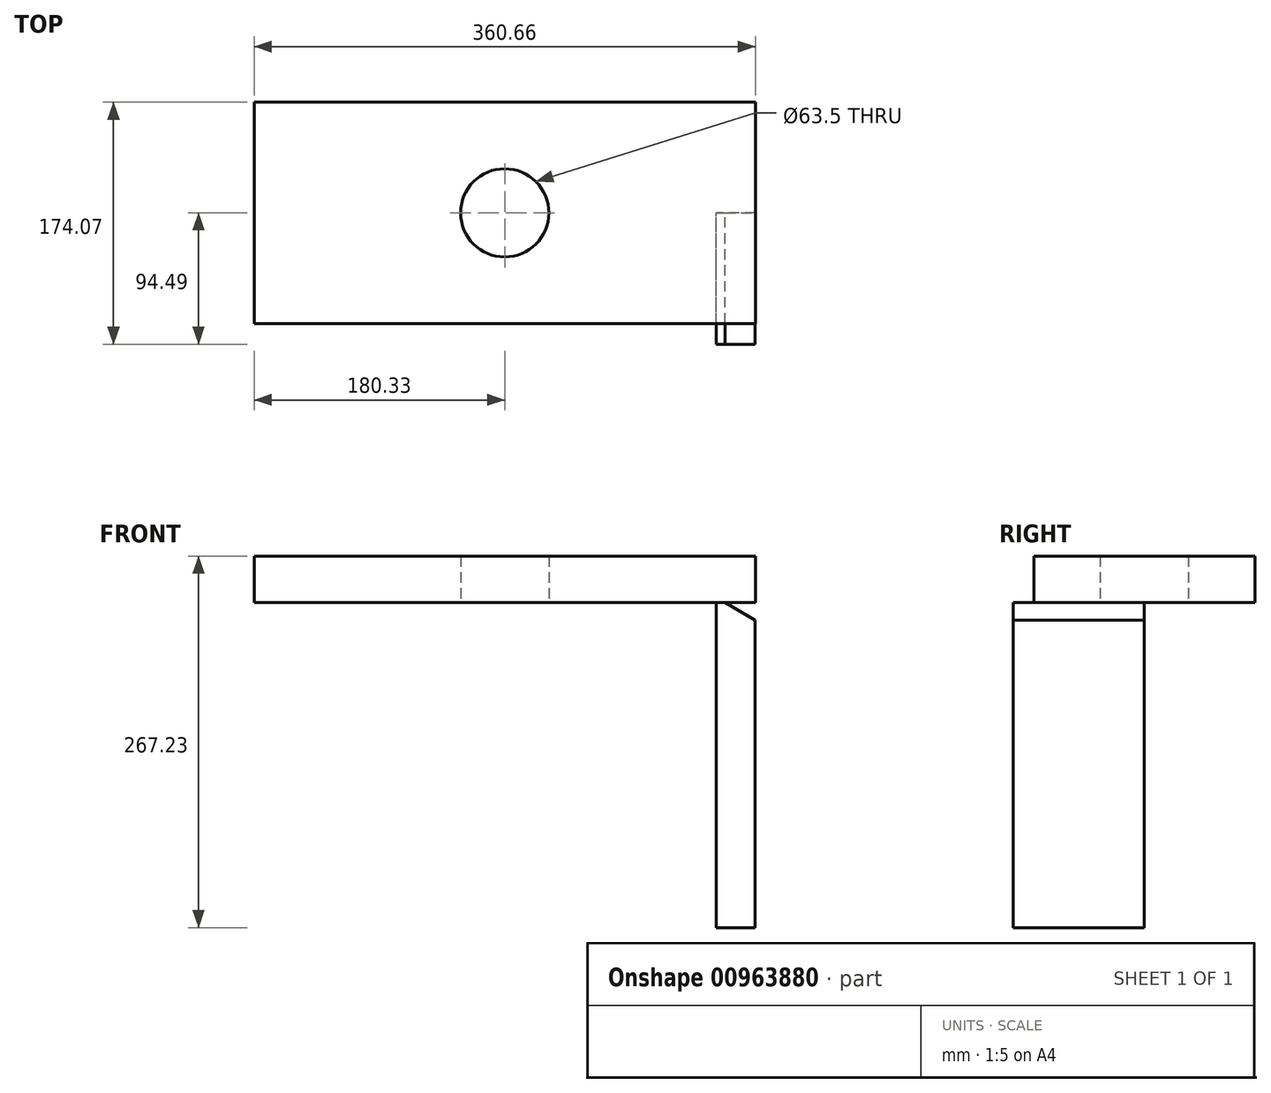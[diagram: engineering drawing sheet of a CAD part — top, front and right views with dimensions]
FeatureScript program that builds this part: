
annotation { "Feature Type Name" : "Feature", "Feature Type Description" : "" }
export const myFeature = defineFeature(function(context is Context, id is Id, definition is map)
    precondition{}
    {
        {
            var Q0;
            Q0=qCreatedBy(makeId("Top.planeOp"),FACE);
            var sketch = newSketch(context, id + "F0", { "sketchPlane" : qUnion([Q0])});
            skLineSegment(sketch, "E0.bottom", {"start": v(-180.33, 79.58) * mm, "end": v(180.33, 79.58) * mm});
            skLineSegment(sketch, "E0.top", {"start": v(-180.33, -79.58) * mm, "end": v(180.33, -79.58) * mm});
            skLineSegment(sketch, "E0.left", {"start": v(-180.33, 79.58) * mm, "end": v(-180.33, -79.58) * mm});
            skLineSegment(sketch, "E0.right", {"start": v(180.33, 79.58) * mm, "end": v(180.33, -79.58) * mm});
            skPoint(sketch, "E0.middle", {"position": v(0, 0) * mm});
            skSolve(sketch);
        }
        {
            var Q0;
            Q0=makeQuery(id+"F0.imprint","IMPRINT",FACE,{"disambiguationData":[TD([[makeQuery(id+"F0.imprint","IMPRINT",EDGE,{"derivedFrom":sQuery(id+"F0.wireOp",EDGE,"E0.bottom")}),-1.0]])]});
            extrude(context, id + "F1", {"entities" : qUnion([Q0]), "depth" : 33.27 * mm, "offsetDistance" : 25.4 * mm});
        }
        {
            var Q0;
            Q0=qCreatedBy(makeId("Front.planeOp"),FACE);
            var sketch = newSketch(context, id + "F2", { "sketchPlane" : qUnion([Q0])});
            skLineSegment(sketch, "E1", {"start": v(152.3, 0) * mm, "end": v(152.3, -233.96) * mm});
            skLineSegment(sketch, "E2", {"start": v(152.3, 0) * mm, "end": v(158.53, 0) * mm});
            skLineSegment(sketch, "E3", {"start": v(158.53, 0) * mm, "end": v(180.22, -12.83) * mm});
            skLineSegment(sketch, "E4", {"start": v(180.22, -12.83) * mm, "end": v(180.22, -233.96) * mm});
            skLineSegment(sketch, "E5", {"start": v(180.22, -233.96) * mm, "end": v(152.3, -233.96) * mm});
            skSolve(sketch);
        }
        {
            var Q0;
            Q0=makeQuery(id+"F2.imprint","IMPRINT",FACE,{"disambiguationData":[TD([[makeQuery(id+"F2.imprint","IMPRINT",EDGE,{"derivedFrom":sQuery(id+"F2.wireOp",EDGE,"E1")}),1.0]])]});
            extrude(context, id + "F3", {"entities" : qUnion([Q0]), "operationType" : NewBodyOperationType.ADD, "depth" : 94.49 * mm, "offsetDistance" : 25.4 * mm});
        }
        {
            var Q0;
            Q0=makeQuery(id+"F1.opExtrude","CAP_FACE",FACE,{"disambiguationData":[OSD([sQuery(id+"F0.wireOp",EDGE,"E0.bottom"),sQuery(id+"F0.wireOp",EDGE,"E0.top"),sQuery(id+"F0.wireOp",EDGE,"E0.left"),sQuery(id+"F0.wireOp",EDGE,"E0.right")])],"isStart":false});
            var sketch = newSketch(context, id + "F4", { "sketchPlane" : qUnion([Q0])});
            skCircle(sketch, "E6", {"center": v(0, 0) * mm, "radius": 39.77 * mm});
            skSolve(sketch);
        }
        {
            var Q0;
            Q0=sQuery(id+"F4.wireOp",VERTEX,"E6.center");
            var Q1;
            Q1=makeQuery(id+"F1.opExtrude","SWEPT_BODY",BODY,{"disambiguationData":[OSD([sQuery(id+"F0.wireOp",EDGE,"E0.bottom"),sQuery(id+"F0.wireOp",EDGE,"E0.top"),sQuery(id+"F0.wireOp",EDGE,"E0.left"),sQuery(id+"F0.wireOp",EDGE,"E0.right")])]});
            hole(context, id + "F5", {"style" : HoleStyle.SIMPLE, "endStyle" : HoleEndStyle.THROUGH, "holeDiameter" : 63.5 * mm, "majorDiameter" : 6.35 * mm, "isTappedThrough" : true, "tappedDepth" : 12.7 * mm, "tapClearance" : 3, "locations" : qUnion([Q0]), "scope" : qUnion([Q1]), "startStyle" : HoleStartStyle.SKETCH});
        }
    });
